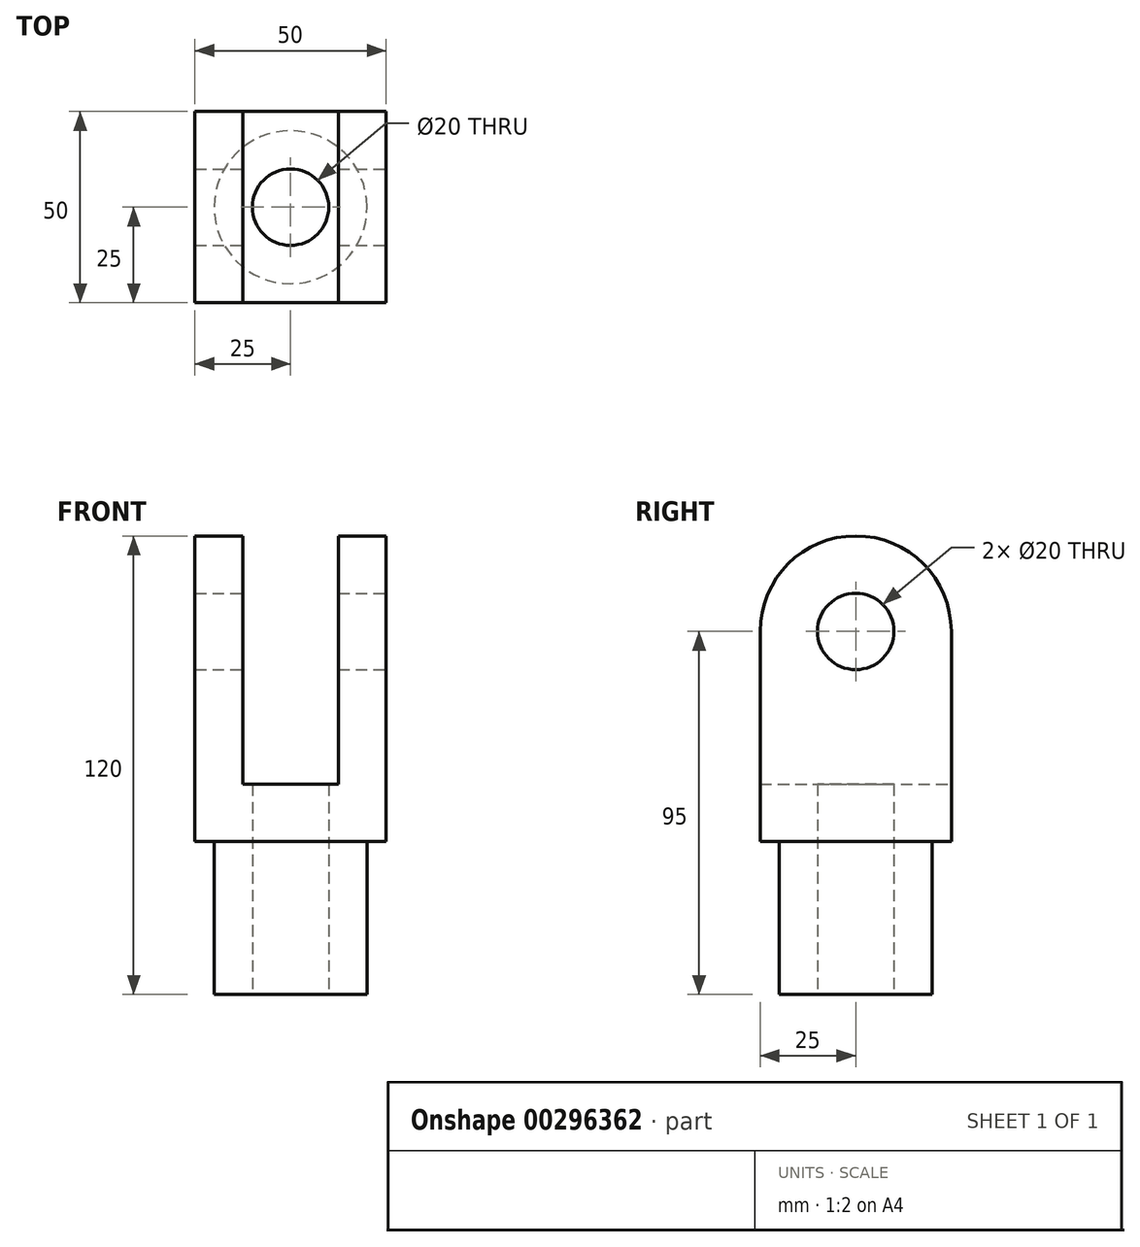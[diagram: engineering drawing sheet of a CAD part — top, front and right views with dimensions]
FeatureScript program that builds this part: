
annotation { "Feature Type Name" : "Feature", "Feature Type Description" : "" }
export const myFeature = defineFeature(function(context is Context, id is Id, definition is map)
    precondition{}
    {
        {
            var Q0;
            Q0=qCreatedBy(makeId("Front.planeOp"),FACE);
            var sketch = newSketch(context, id + "F0", { "sketchPlane" : qUnion([Q0])});
            skLineSegment(sketch, "E0", {"start": v(0, 0) * mm, "end": v(-25, 0) * mm});
            skLineSegment(sketch, "E1", {"start": v(-25, 0) * mm, "end": v(-25, 80) * mm});
            skLineSegment(sketch, "E2", {"start": v(-25, 80) * mm, "end": v(-12.5, 80) * mm});
            skLineSegment(sketch, "E3", {"start": v(-12.5, 80) * mm, "end": v(-12.5, 15) * mm});
            skLineSegment(sketch, "E4", {"start": v(-12.5, 15) * mm, "end": v(0, 15) * mm});
            skLineSegment(sketch, "E5.MirrorCS", {"start": v(0, 0) * mm, "end": v(25, 0) * mm});
            skLineSegment(sketch, "E6.MirrorCS", {"start": v(25, 80) * mm, "end": v(12.5, 80) * mm});
            skLineSegment(sketch, "E7.MirrorCS", {"start": v(12.5, 15) * mm, "end": v(0, 15) * mm});
            skLineSegment(sketch, "E8.MirrorCS", {"start": v(25, 0) * mm, "end": v(25, 80) * mm});
            skLineSegment(sketch, "E9.MirrorCS", {"start": v(12.5, 80) * mm, "end": v(12.5, 15) * mm});
            skSolve(sketch);
        }
        {
            var Q0;
            Q0 = qSketchRegion(id + "F0", true);
            extrude(context, id + "F1", {"entities" : qUnion([Q0]), "depth" : 50 * mm});
        }
        {
            var Q0;
            Q0=makeQuery(id+"F1.opExtrude","CAP_EDGE",EDGE,{"disambiguationData":[OSD([sQuery(id+"F0.wireOp",EDGE,"E6.MirrorCS")])],"isStart":true});
            var Q1;
            Q1=makeQuery(id+"F1.opExtrude","CAP_EDGE",EDGE,{"disambiguationData":[OSD([sQuery(id+"F0.wireOp",EDGE,"E2")])],"isStart":true});
            var Q2;
            Q2=makeQuery(id+"F1.opExtrude","CAP_EDGE",EDGE,{"disambiguationData":[OSD([sQuery(id+"F0.wireOp",EDGE,"E2")])],"isStart":false});
            var Q3;
            Q3=makeQuery(id+"F1.opExtrude","CAP_EDGE",EDGE,{"disambiguationData":[OSD([sQuery(id+"F0.wireOp",EDGE,"E6.MirrorCS")])],"isStart":false});
            fillet(context, id + "F2", {"entities" : qUnion([Q0, Q1, Q2, Q3]), "radius" : 25 * mm, "tangentPropagation" : true, "allowEdgeOverflow" : false});
        }
        {
            var Q0;
            Q0=makeQuery(id+"F1.opExtrude","SWEPT_FACE",FACE,{"disambiguationData":[OSD([sQuery(id+"F0.wireOp",EDGE,"E8.MirrorCS")])]});
            var sketch = newSketch(context, id + "F3", { "sketchPlane" : qUnion([Q0])});
            skCircle(sketch, "E10", {"center": v(-25, 55) * mm, "radius": 10 * mm});
            skSolve(sketch);
        }
        {
            var Q0;
            Q0=sQuery(id+"F3.wireOp",VERTEX,"E10.center");
            var Q1;
            Q1=makeQuery(id+"F1.opExtrude","SWEPT_BODY",BODY,{"disambiguationData":[OSD([sQuery(id+"F0.wireOp",EDGE,"E0"),sQuery(id+"F0.wireOp",EDGE,"E1"),sQuery(id+"F0.wireOp",EDGE,"E2"),sQuery(id+"F0.wireOp",EDGE,"E3"),sQuery(id+"F0.wireOp",EDGE,"E4"),sQuery(id+"F0.wireOp",EDGE,"E5.MirrorCS"),sQuery(id+"F0.wireOp",EDGE,"E6.MirrorCS"),sQuery(id+"F0.wireOp",EDGE,"E7.MirrorCS"),sQuery(id+"F0.wireOp",EDGE,"E8.MirrorCS"),sQuery(id+"F0.wireOp",EDGE,"E9.MirrorCS")])]});
            hole(context, id + "F4", {"style" : HoleStyle.SIMPLE, "endStyle" : HoleEndStyle.THROUGH, "holeDiameter" : 20 * mm, "tappedDepth" : 12 * mm, "tapClearance" : 3, "locations" : qUnion([Q0]), "scope" : qUnion([Q1])});
        }
        {
            var Q0;
            Q0=makeQuery(id+"F1.opExtrude","SWEPT_FACE",FACE,{"disambiguationData":[OSD([sQuery(id+"F0.wireOp",EDGE,"E0"),sQuery(id+"F0.wireOp",EDGE,"E5.MirrorCS")])]});
            var sketch = newSketch(context, id + "F5", { "sketchPlane" : qUnion([Q0])});
            skCircle(sketch, "E11", {"center": v(0, 25) * mm, "radius": 20 * mm});
            skSolve(sketch);
        }
        {
            var Q0;
            Q0=makeQuery(id+"F5.imprint","IMPRINT",FACE,{"disambiguationData":[TD([[makeQuery(id+"F5.imprint","IMPRINT",EDGE,{"derivedFrom":sQuery(id+"F5.wireOp",EDGE,"E11")}),1.0]])]});
            extrude(context, id + "F6", {"entities" : qUnion([Q0]), "operationType" : NewBodyOperationType.ADD, "depth" : 40 * mm});
        }
        {
            var Q0;
            Q0=makeQuery(id+"F6.opExtrude","CAP_FACE",FACE,{"disambiguationData":[OSD([sQuery(id+"F5.wireOp",EDGE,"E11")])],"isStart":false});
            var sketch = newSketch(context, id + "F7", { "sketchPlane" : qUnion([Q0])});
            skCircle(sketch, "E12", {"center": v(0, 25) * mm, "radius": 10 * mm});
            skSolve(sketch);
        }
        {
            var Q0;
            Q0=sQuery(id+"F7.wireOp",VERTEX,"E12.center");
            var Q1;
            Q1=makeQuery(id+"F1.opExtrude","SWEPT_BODY",BODY,{"disambiguationData":[OSD([sQuery(id+"F0.wireOp",EDGE,"E0"),sQuery(id+"F0.wireOp",EDGE,"E1"),sQuery(id+"F0.wireOp",EDGE,"E2"),sQuery(id+"F0.wireOp",EDGE,"E3"),sQuery(id+"F0.wireOp",EDGE,"E4"),sQuery(id+"F0.wireOp",EDGE,"E5.MirrorCS"),sQuery(id+"F0.wireOp",EDGE,"E6.MirrorCS"),sQuery(id+"F0.wireOp",EDGE,"E7.MirrorCS"),sQuery(id+"F0.wireOp",EDGE,"E8.MirrorCS"),sQuery(id+"F0.wireOp",EDGE,"E9.MirrorCS")])]});
            hole(context, id + "F8", {"style" : HoleStyle.SIMPLE, "endStyle" : HoleEndStyle.THROUGH, "holeDiameter" : 20 * mm, "tappedDepth" : 12 * mm, "tapClearance" : 3, "locations" : qUnion([Q0]), "scope" : qUnion([Q1])});
        }
    });
